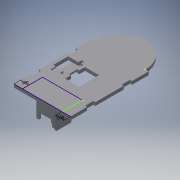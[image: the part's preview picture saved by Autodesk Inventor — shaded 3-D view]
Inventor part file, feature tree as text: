
AUTODESK INVENTOR PART (.ipt)
format: ipt  version: 2016 (Build 200138000, 138)  size: 475,648 bytes
history: native  units: in
note: dims shown in document units (in); Inventor stores cm internally (conversion verified against a paired STEP export)
features: reference x37, extrude x24, sketch x24, plane x6, projected_geometry x1
ambient origin geometry x8: Origin, YZ Plane, XZ Plane, XY Plane, X Axis, Y Axis, Z Axis, Center Point
bodies: Solid1 (feature_tree)
feature tree (92):
  extrude  "Extrusion1"  Depth=3.0in
  extrude  "Extrusion2"  Depth=0.0787in
  extrude  "Extrusion3"  Depth=1.0in
  extrude  "Extrusion5"  Depth=1.0in TaperAngle=0.0deg
  plane  "Work Plane1"
  extrude  "Extrusion6"  Depth=0.0787in
  extrude  "Extrusion9"  Depth=0.0787in
  extrude  "Extrusion14"  Depth=0.1575in
  extrude  "Extrusion15"  Depth=1.25in
  plane  "Work Plane2"
  extrude  "Extrusion16"  Depth=0.1575in
  extrude  "Extrusion17"  Depth=0.9201in TaperAngle=0.0deg
  extrude  "Extrusion18"  Depth=0.1969in
  plane  "Work Plane3"
  extrude  "Extrusion20"  Depth=0.1969in TaperAngle=0.0deg
  extrude  "Extrusion21"  Depth=0.1181in TaperAngle=0.0deg
  plane  "Work Plane4"
  plane  "Work Plane5"
  extrude  "Extrusion23"  Depth=0.1181in
  extrude  "Extrusion24"  Depth=0.1969in TaperAngle=0.0deg
  plane  "Work Plane6"
  extrude  "Extrusion25"  Depth=0.35in
  extrude  "Extrusion26"  Depth=0.2in
  extrude  "Extrusion27"  Depth=0.1969in TaperAngle=0.0deg
  extrude  "Extrusion28"  Depth=1.5in
  extrude  "Extrusion29"  Depth=0.7in
  extrude  "Extrusion30"  Depth=0.1181in TaperAngle=0.0deg
  extrude  "Extrusion31"  Depth=1.0in
  extrude  "Extrusion34"  Depth=0.5in
  sketch  "Sketch36"  dims[d105=0.1181in d106=0.5in]
  extrude  "Extrusion35"  Depth=0.5in
  sketch  "Sketch1"  dims[d0=4.5in d1=3.0in]
  sketch  "Sketch2"  dims[d2=0.1969in d3=0.0in d5=0.0787in]
  reference  "Reference1"
  reference  "Reference2"
  sketch  "Sketch3"  dims[d6=1.0in d7=0.0in d8=1.0827in]
  sketch  "Sketch5"  dims[d9=0.3937in d10=1.0in d11=0.0in]
  reference  "Reference14"
  reference  "Reference15"
  reference  "Reference16"
  reference  "Reference17"
  reference  "Reference18"
  sketch  "Sketch6"  dims[d12=0.0787in d23=0.0098in]
  reference  "Reference19"
  sketch  "Sketch9"  dims[d24=0.1575in d25=0.0787in]
  projected_geometry  "Projected Loop2"
  sketch  "Sketch14"  dims[d26=0.0098in d27=0.1575in]
  sketch  "Sketch15"  dims[d28=0.1181in d29=0.0in d30=1.25in]
  sketch  "Sketch16"  dims[d31=0.1575in d32=0.1575in]
  reference  "Reference30"
  sketch  "Sketch17"  dims[d33=0.1181in d34=0.0in d46=0.9201in d47=0.0in]
  reference  "Reference31"
  reference  "Reference32"
  reference  "Reference33"
  reference  "Reference35"
  reference  "Reference36"
  reference  "Reference37"
  reference  "Reference38"
  reference  "Reference39"
  reference  "Reference40"
  reference  "Reference41"
  reference  "Reference42"
  reference  "Reference43"
  reference  "Reference44"
  reference  "Reference45"
  reference  "Reference46"
  reference  "Reference47"
  reference  "Reference48"
  reference  "Reference49"
  sketch  "Sketch20"  dims[d58=0.1969in d59=0.1969in]
  reference  "Reference50"
  sketch  "Sketch21"  dims[d60=0.1969in d61=0.1969in d62=0.0in]
  sketch  "Sketch23"  dims[d63=1.0in d64=0.0in d65=0.1181in d66=0.0in]
  reference  "Reference53"
  reference  "Reference54"
  sketch  "Sketch24"  dims[d67=0.1969in d68=0.0in d69=0.1181in]
  sketch  "Sketch25"  dims[d70=0.1181in d71=0.1969in d72=0.0in]
  reference  "Reference55"
  reference  "Reference56"
  sketch  "Sketch26"  dims[d75=0.0394in d76=0.35in]
  reference  "Reference57"
  reference  "Reference58"
  sketch  "Sketch28"  dims[d77=0.1628in d78=0.2in]
  sketch  "Sketch29"  dims[d79=0.0787in d80=0.0in d81=0.1969in d82=0.0in]
  sketch  "Sketch30"  dims[d89=1.5in d90=1.5in]
  reference  "Reference59"
  sketch  "Sketch31"  dims[d91=0.1181in d92=0.0in d93=0.7in]
  sketch  "Sketch32"  dims[d94=1.26in d95=0.0in d96=0.1181in d97=0.0in]
  sketch  "Sketch35"  dims[d98=0.1181in d99=0.0in d104=1.0in]
  reference  "Reference61"
  sketch  "Sketch37"  dims[d107=1.0in d108=0.5in d109=10.0in d110=0.0in d111=0.0197in d112=0.0197in d113=0.325in d114=0.197in d115=0.0in d116=0.1969in d117=0.1969in d118=0.1181in d119=0.1969in d120=0.0in d121=0.1575in d122=0.0in d123=0.1in d124=0.0in d132=1.0in d133=0.0in d134=0.5in d135=0.5in d136=0.0039in d137=0.0039in d138=0.0984in d139=0.0984in d140=0.0039in d141=0.0984in d142=1.61in d143=0.0in]
  reference  "Reference62"
